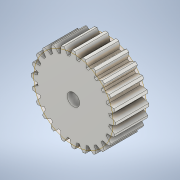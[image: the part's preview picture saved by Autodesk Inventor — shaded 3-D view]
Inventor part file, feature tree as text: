
AUTODESK INVENTOR PART (.ipt)
format: ipt  version: 2021 (Build 250183000, 183)  size: 250,880 bytes
history: native  units: mm (DEFAULTED — no unit token found)
features: plane x3, other x3, sketch x3, extrude x1, hole x1
ambient origin geometry x8: Origin, YZ Plane, XZ Plane, XY Plane, X Axis, Y Axis, Z Axis, Center Point
bodies: Solid1 (feature_tree)
feature tree (11):
  extrude  "Extrusion1"  Depth=8.0mm TaperAngle=0.0deg
  plane  "Work Plane2"
  plane  "Work Plane8"
  plane  "Work Plane9"
  other  "Spur Gear"
  hole  "Hole1"  [1 undecoded]
  sketch  "Sketch1"  dims[d0=20.48mm d1=8.0mm d2=0.0mm]
  sketch  "Sketch2"  dims[d3=19.2mm d4=10.0mm d5=0.0mm]
  other  "Srf1"
  sketch  "Sketch3"  dims[d16=28.8mm d17=0.0mm d34=1.308997mm d39=0.0mm d41=0.0mm d43=28.8mm d46=28.8mm d47=0.0mm d48=0.0mm d49=3.0mm d50=3.0mm d51=6.0mm d52=4.0mm d53=2.0mm d54=90.0deg d55=8.0mm d56=20.594885mm]
  other  "Pitch Diameter"
note: 1 required parameter value undecoded (feature->parameter linkage not recoverable at this tier; creation-order binding heuristic only, values carry confidence <= 0.55)
